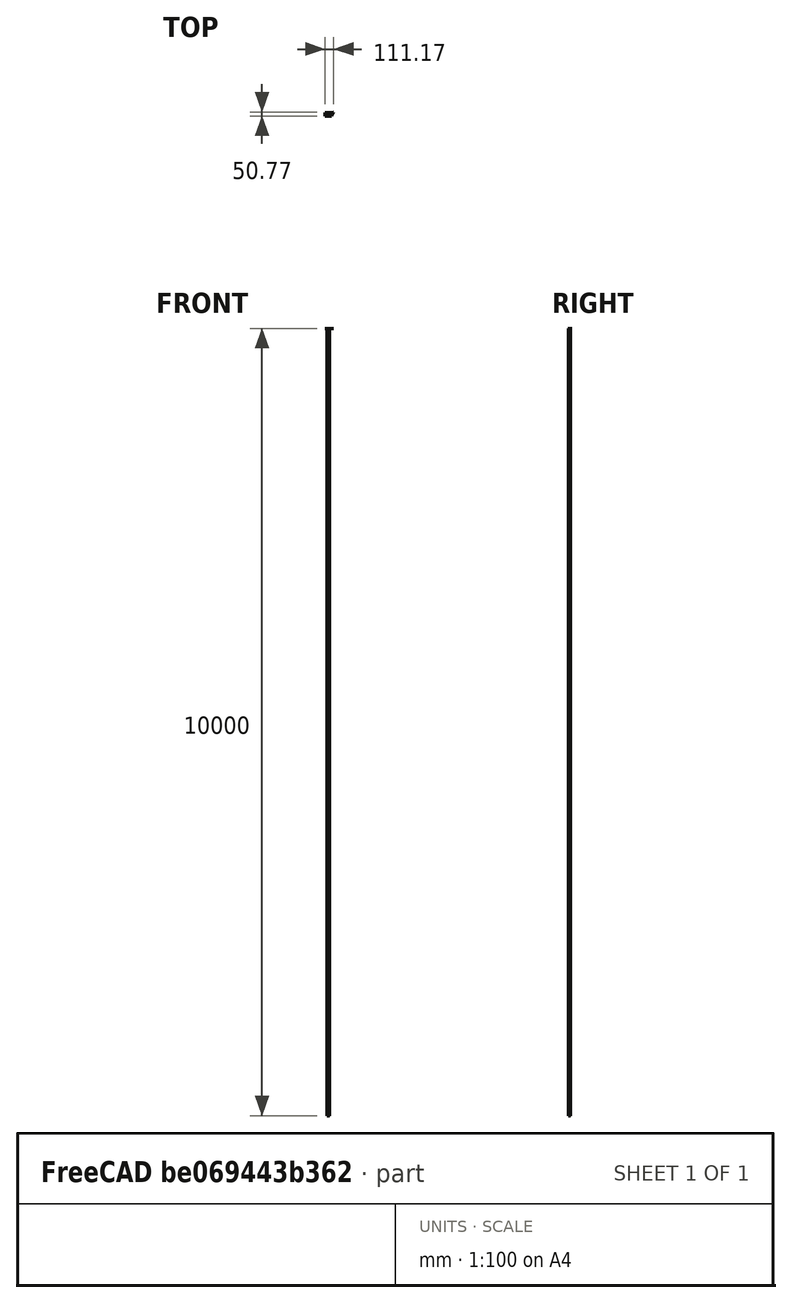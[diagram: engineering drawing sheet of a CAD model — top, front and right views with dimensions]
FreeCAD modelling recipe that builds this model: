
FCSTD DOCUMENT  (FreeCAD 0.14R3702 (Git))
Label: dock_tableta2
License: CC-BY 3.0
LicenseURL: http://creativecommons.org/licenses/by/3.0/
objects: Sketcher::SketchObject×2, PartDesign::Pad×1, PartDesign::Pocket×1
note: 6 computed .brp shape members not serialized (recipe doc carries the construction recipe); baked Part::Feature solids carry a one-line shape summary decoded from their .brp

FEATURE [Sketcher::SketchObject] Sketch
  sketch-geometry (4):
    g0: LineSegment StartX=-68.6792 StartY=16.8358 StartZ=0 EndX=42.4903 EndY=28.8613 EndZ=0
    g1: LineSegment StartX=42.4903 StartY=28.8613 StartZ=0 EndX=13.3617 EndY=-21.9132 EndZ=0
    g2: LineSegment StartX=13.3617 StartY=-21.9132 StartZ=0 EndX=-68.6792 EndY=-21.9132 EndZ=0
    g3: LineSegment StartX=-68.6792 StartY=-21.9132 StartZ=0 EndX=-68.6792 EndY=16.8358 EndZ=0
  constraints (6):
    c: Coincident(g0,g1)
    c: Coincident(g1,g2)
    c: Horizontal(g2)
    c: Coincident(g2,g3)
    c: Coincident(g3,g0)
    c: Vertical(g3)
FEATURE [PartDesign::Pad] Pad
  Length = 2
  Length2 = 100
  Sketch = -> Sketch
  Type = 0
FEATURE [Sketcher::SketchObject] Sketch001
  Placement = pos=(0,0,2) rot=(0,0,1;0rad)
  Support = -> Pad [Face6]
  sketch-geometry (1):
    g0: Circle CenterX=-27.5251 CenterY=-3.47405 CenterZ=0 NormalX=0 NormalY=0 NormalZ=1 Radius=13.8266
FEATURE [PartDesign::Pocket] Pocket
  Length = 5
  Sketch = -> Sketch001
  Type = 1
